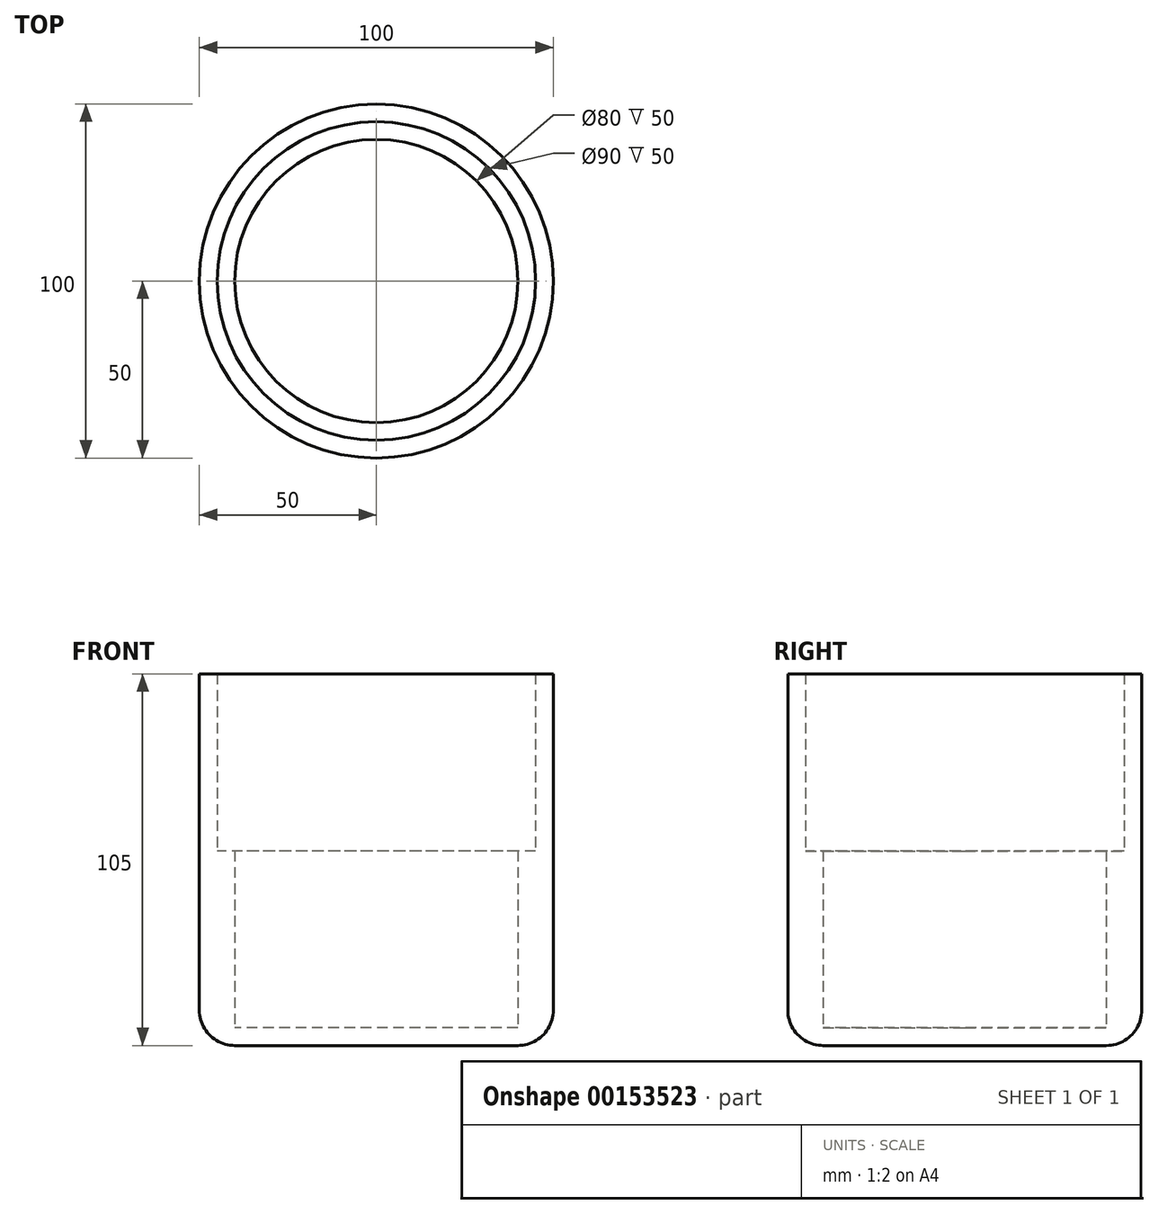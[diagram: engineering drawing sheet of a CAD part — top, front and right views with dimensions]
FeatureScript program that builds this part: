
annotation { "Feature Type Name" : "Feature", "Feature Type Description" : "" }
export const myFeature = defineFeature(function(context is Context, id is Id, definition is map)
    precondition{}
    {
        {
            var Q0;
            Q0=qCreatedBy(makeId("Top.planeOp"),FACE);
            var sketch = newSketch(context, id + "F0", { "sketchPlane" : qUnion([Q0])});
            skCircle(sketch, "E0", {"center": v(0, 0) * mm, "radius": 40 * mm});
            skCircle(sketch, "E1", {"center": v(0, 0) * mm, "radius": 45 * mm});
            skCircle(sketch, "E2", {"center": v(0, 0) * mm, "radius": 50 * mm});
            skSolve(sketch);
        }
        {
            var Q0;
            Q0=makeQuery(id+"F0.imprint","IMPRINT",FACE,{"disambiguationData":[TD([[makeQuery(id+"F0.imprint","IMPRINT",EDGE,{"derivedFrom":sQuery(id+"F0.wireOp",EDGE,"E0")}),-1.0]])]});
            extrude(context, id + "F1", {"entities" : qUnion([Q0]), "depth" : 50 * mm});
        }
        {
            var Q0;
            Q0 = qSketchRegion(id + "F0", true);
            extrude(context, id + "F2", {"entities" : qUnion([Q0]), "operationType" : NewBodyOperationType.ADD, "depth" : 100 * mm});
        }
        {
            var Q0;
            Q0=makeQuery(id+"F0.imprint","IMPRINT",FACE,{"disambiguationData":[TD([[makeQuery(id+"F0.imprint","IMPRINT",EDGE,{"derivedFrom":sQuery(id+"F0.wireOp",EDGE,"E0")}),1.0]])]});
            var Q1;
            Q1=makeQuery(id+"F0.imprint","IMPRINT",FACE,{"disambiguationData":[TD([[makeQuery(id+"F0.imprint","IMPRINT",EDGE,{"derivedFrom":sQuery(id+"F0.wireOp",EDGE,"E0")}),-1.0]])]});
            var Q2;
            Q2=makeQuery(id+"F0.imprint","IMPRINT",FACE,{"disambiguationData":[TD([[makeQuery(id+"F0.imprint","IMPRINT",EDGE,{"derivedFrom":sQuery(id+"F0.wireOp",EDGE,"E1")}),-1.0]])]});
            extrude(context, id + "F3", {"entities" : qUnion([Q0, Q1, Q2]), "operationType" : NewBodyOperationType.ADD, "oppositeDirection" : true, "depth" : 5 * mm});
        }
        {
            var Q0;
            Q0=makeQuery(id+"F3.opExtrude","CAP_EDGE",EDGE,{"disambiguationData":[OSD([sQuery(id+"F0.wireOp",EDGE,"E2")])],"isStart":false});
            fillet(context, id + "F4", {"entities" : qUnion([Q0]), "radius" : 10 * mm, "tangentPropagation" : true, "allowEdgeOverflow" : false});
        }
    });
